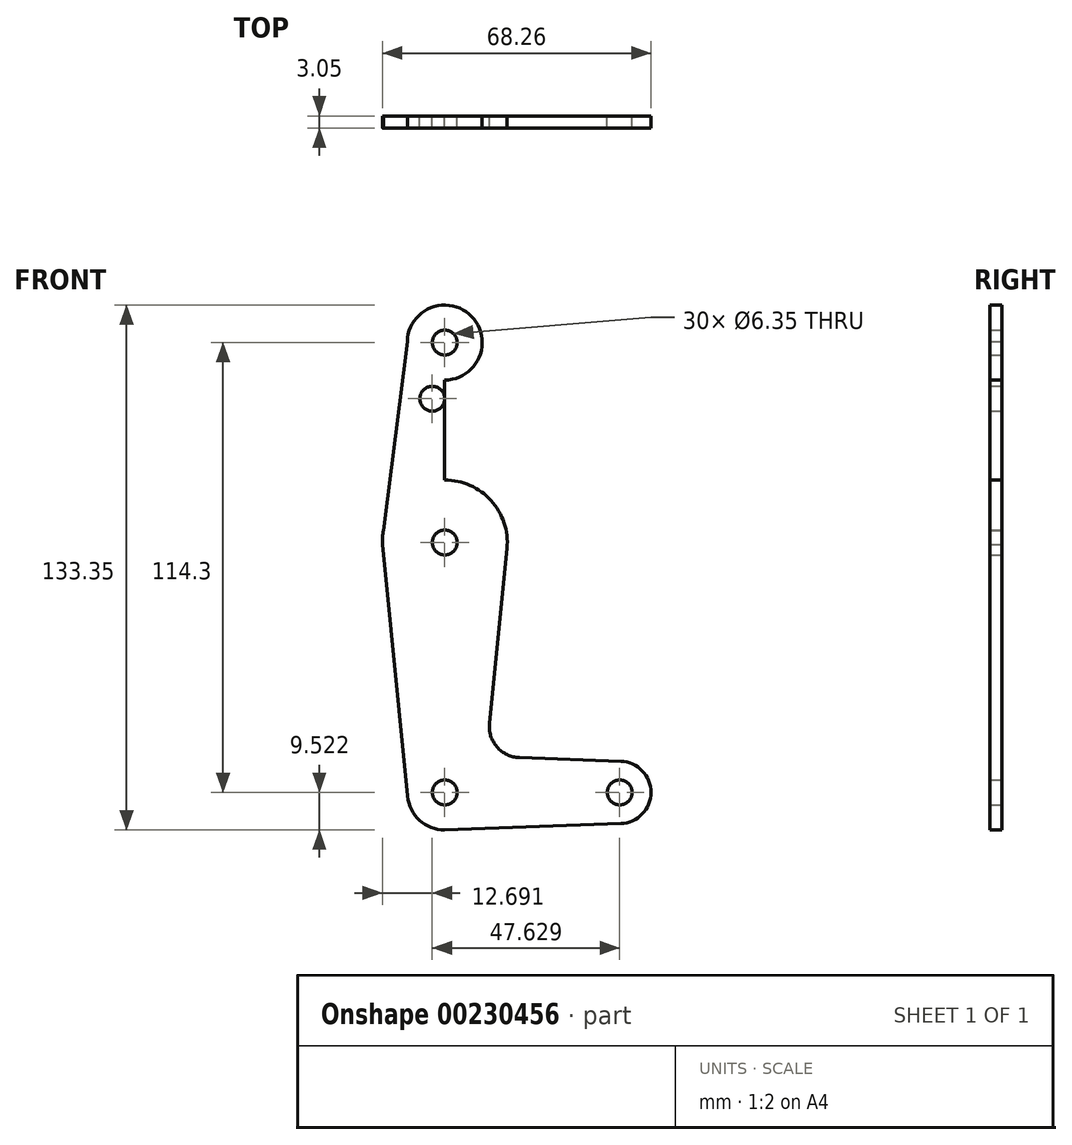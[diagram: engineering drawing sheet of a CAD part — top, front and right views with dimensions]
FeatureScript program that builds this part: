
annotation { "Feature Type Name" : "Feature", "Feature Type Description" : "" }
export const myFeature = defineFeature(function(context is Context, id is Id, definition is map)
    precondition{}
    {
        {
            var Q0;
            Q0=qCreatedBy(makeId("Front.planeOp"),FACE);
            var sketch = newSketch(context, id + "F0", { "sketchPlane" : qUnion([Q0])});
            skLineSegment(sketch, "E0", {"start": v(0, 73.32) * mm, "end": v(0, -40.98) * mm});
            skLineSegment(sketch, "E1", {"start": v(0, -40.98) * mm, "end": v(44.45, -40.98) * mm});
            skCircle(sketch, "E2", {"center": v(0, 73.32) * mm, "radius": 9.53 * mm});
            skCircle(sketch, "E3", {"center": v(0, -40.98) * mm, "radius": 9.53 * mm});
            skCircle(sketch, "E4", {"center": v(44.45, -40.98) * mm, "radius": 7.94 * mm});
            skLineSegment(sketch, "E5", {"start": v(0, -40.98) * mm, "end": v(0, 22.52) * mm});
            skCircle(sketch, "E6", {"center": v(0, 22.52) * mm, "radius": 15.88 * mm});
            skLineSegment(sketch, "E7", {"start": v(-9.52, 73.56) * mm, "end": v(-15.85, 23.48) * mm});
            skLineSegment(sketch, "E8", {"start": v(9.52, 73.56) * mm, "end": v(15.85, 23.48) * mm});
            skLineSegment(sketch, "E9", {"start": v(-15.87, 22.05) * mm, "end": v(-9.48, -41.92) * mm});
            skLineSegment(sketch, "E10", {"start": v(15.8, 21) * mm, "end": v(11.34, -23.39) * mm});
            skLineSegment(sketch, "E11", {"start": v(18.97, -32.13) * mm, "end": v(44.73, -33.05) * mm});
            skLineSegment(sketch, "E12", {"start": v(0, -50.5) * mm, "end": v(44.73, -48.91) * mm});
            skCircle(sketch, "E13", {"center": v(0, 73.32) * mm, "radius": 3.18 * mm});
            skCircle(sketch, "E14", {"center": v(0, 22.52) * mm, "radius": 3.18 * mm});
            skCircle(sketch, "E15", {"center": v(0, -40.98) * mm, "radius": 3.18 * mm});
            skCircle(sketch, "E16", {"center": v(44.45, -40.98) * mm, "radius": 3.18 * mm});
            skLineSegment(sketch, "E17", {"start": v(0, 22.52) * mm, "end": v(0, 59.05) * mm});
            skCircle(sketch, "E18", {"center": v(-3.18, 59.05) * mm, "radius": 3.18 * mm});
            skPoint(sketch, "E19.newPointB", {"position": v(0, -31.45) * mm});
            skArc(sketch, "E19.filletArc", {"start": v(11.34, -23.39) * mm, "mid": v(13.26, -29.41) * mm, "end": v(18.97, -32.13) * mm});
            skSolve(sketch);
        }
        {
            var Q0;
            {var subQ0=sQuery(id+"F0.wireOp",EDGE,"E12");var subQ1=sQuery(id+"F0.wireOp",EDGE,"E3");var subQ2=makeQuery(id+"F0.imprint","INTERSECT",VERTEX,{"disambiguationData":[OD(0.0)],"derivedFrom":[subQ1,subQ0]});Q0=makeQuery(id+"F0.imprint","IMPRINT",FACE,{"disambiguationData":[TD([[makeQuery(id+"F0.imprint","IMPRINT",EDGE,{"disambiguationData":[TD([[subQ2,-1.0]])],"derivedFrom":subQ1}),1.0]])]});}
            var Q1;
            {var subQ0=sQuery(id+"F0.wireOp",EDGE,"E8");var subQ1=sQuery(id+"F0.wireOp",EDGE,"E6");var subQ2=makeQuery(id+"F0.imprint","INTERSECT",VERTEX,{"disambiguationData":[OD(0.0)],"derivedFrom":[subQ1,subQ0]});Q1=makeQuery(id+"F0.imprint","IMPRINT",FACE,{"disambiguationData":[TD([[makeQuery(id+"F0.imprint","IMPRINT",EDGE,{"disambiguationData":[TD([[subQ2,-1.0]])],"derivedFrom":subQ1}),1.0]])]});}
            var Q2;
            {var subQ0=sQuery(id+"F0.wireOp",EDGE,"E7");var subQ1=sQuery(id+"F0.wireOp",EDGE,"E6");var subQ2=makeQuery(id+"F0.imprint","INTERSECT",VERTEX,{"disambiguationData":[OD(0.0)],"derivedFrom":[subQ1,subQ0]});Q2=makeQuery(id+"F0.imprint","IMPRINT",FACE,{"disambiguationData":[TD([[makeQuery(id+"F0.imprint","IMPRINT",EDGE,{"disambiguationData":[TD([[subQ2,1.0]])],"derivedFrom":subQ1}),1.0]])]});}
            var Q3;
            {var subQ0=sQuery(id+"F0.wireOp",EDGE,"E9");var subQ1=sQuery(id+"F0.wireOp",EDGE,"E6");var subQ2=makeQuery(id+"F0.imprint","INTERSECT",VERTEX,{"disambiguationData":[OD(0.0)],"derivedFrom":[subQ1,subQ0]});Q3=makeQuery(id+"F0.imprint","IMPRINT",FACE,{"disambiguationData":[TD([[makeQuery(id+"F0.imprint","IMPRINT",EDGE,{"disambiguationData":[TD([[subQ2,-1.0]])],"derivedFrom":subQ1}),1.0]])]});}
            var Q4;
            {var subQ0=sQuery(id+"F0.wireOp",EDGE,"E10");var subQ1=sQuery(id+"F0.wireOp",EDGE,"E6");var subQ2=makeQuery(id+"F0.imprint","INTERSECT",VERTEX,{"disambiguationData":[OD(0.0)],"derivedFrom":[subQ1,subQ0]});Q4=makeQuery(id+"F0.imprint","IMPRINT",FACE,{"disambiguationData":[TD([[makeQuery(id+"F0.imprint","IMPRINT",EDGE,{"disambiguationData":[TD([[subQ2,1.0]])],"derivedFrom":subQ1}),1.0]])]});}
            var Q5;
            {var subQ3=sQuery(id+"F0.wireOp",EDGE,"E17");var subQ7=sQuery(id+"F0.wireOp",EDGE,"E0");var subQ9=makeQuery(id+"F0.imprint","INTERSECT",VERTEX,{"derivedFrom":[subQ7,subQ3]});Q5=makeQuery(id+"F0.imprint","IMPRINT",FACE,{"disambiguationData":[TD([[makeQuery(id+"F0.imprint","IMPRINT",EDGE,{"disambiguationData":[TD([[subQ9,1.0]])],"derivedFrom":subQ7}),1.0]])]});}
            var Q6;
            {var subQ0=sQuery(id+"F0.wireOp",EDGE,"E4");var subQ1=sQuery(id+"F0.wireOp",EDGE,"E1");var subQ2=makeQuery(id+"F0.imprint","INTERSECT",VERTEX,{"derivedFrom":[subQ1,subQ0]});Q6=makeQuery(id+"F0.imprint","IMPRINT",FACE,{"disambiguationData":[TD([[makeQuery(id+"F0.imprint","IMPRINT",EDGE,{"disambiguationData":[TD([[subQ2,1.0]])],"derivedFrom":subQ1}),-1.0]])]});}
            var Q7;
            Q7=makeQuery(id+"F0.imprint","IMPRINT",FACE,{"disambiguationData":[TD([[makeQuery(id+"F0.imprint","IMPRINT",EDGE,{"derivedFrom":sQuery(id+"F0.wireOp",EDGE,"E13")}),-1.0]])]});
            var Q8;
            {var subQ0=sQuery(id+"F0.wireOp",EDGE,"E9");var subQ1=sQuery(id+"F0.wireOp",EDGE,"E3");var subQ2=makeQuery(id+"F0.imprint","INTERSECT",VERTEX,{"derivedFrom":[subQ1,subQ0]});Q8=makeQuery(id+"F0.imprint","IMPRINT",FACE,{"disambiguationData":[TD([[makeQuery(id+"F0.imprint","IMPRINT",EDGE,{"disambiguationData":[TD([[subQ2,1.0]])],"derivedFrom":subQ1}),-1.0]])]});}
            var Q9;
            Q9=makeQuery(id+"F0.imprint","IMPRINT",FACE,{"disambiguationData":[TD([[makeQuery(id+"F0.imprint","IMPRINT",EDGE,{"derivedFrom":sQuery(id+"F0.wireOp",EDGE,"E16")}),-1.0]])]});
            var Q10;
            Q10=makeQuery(id+"F0.imprint","IMPRINT",FACE,{"disambiguationData":[TD([[makeQuery(id+"F0.imprint","IMPRINT",EDGE,{"derivedFrom":sQuery(id+"F0.wireOp",EDGE,"E18")}),-1.0]])]});
            var Q11;
            {var subQ0=sQuery(id+"F0.wireOp",EDGE,"E11");Q11=makeQuery(id+"F0.imprint","IMPRINT",FACE,{"disambiguationData":[TD([[makeQuery(id+"F0.imprint","IMPRINT",EDGE,{"derivedFrom":subQ0}),-1.0]])]});}
            var Q12;
            {var subQ1=sQuery(id+"F0.wireOp",EDGE,"E6");var subQ7=sQuery(id+"F0.wireOp",EDGE,"E5");var subQ8=makeQuery(id+"F0.imprint","INTERSECT",VERTEX,{"derivedFrom":[subQ7,subQ1]});Q12=makeQuery(id+"F0.imprint","IMPRINT",FACE,{"disambiguationData":[TD([[makeQuery(id+"F0.imprint","IMPRINT",EDGE,{"disambiguationData":[TD([[subQ8,-1.0]])],"derivedFrom":subQ7}),-1.0]])]});}
            var Q13;
            {var subQ1=sQuery(id+"F0.wireOp",EDGE,"E6");var subQ3=sQuery(id+"F0.wireOp",EDGE,"E5");var subQ4=makeQuery(id+"F0.imprint","INTERSECT",VERTEX,{"derivedFrom":[subQ3,subQ1]});Q13=makeQuery(id+"F0.imprint","IMPRINT",FACE,{"disambiguationData":[TD([[makeQuery(id+"F0.imprint","IMPRINT",EDGE,{"disambiguationData":[TD([[subQ4,-1.0]])],"derivedFrom":subQ3}),1.0]])]});}
            var Q14;
            {var subQ3=sQuery(id+"F0.wireOp",EDGE,"E1");var subQ7=sQuery(id+"F0.wireOp",EDGE,"E15");var subQ8=makeQuery(id+"F0.imprint","INTERSECT",VERTEX,{"derivedFrom":[subQ3,subQ7]});Q14=makeQuery(id+"F0.imprint","IMPRINT",FACE,{"disambiguationData":[TD([[makeQuery(id+"F0.imprint","IMPRINT",EDGE,{"disambiguationData":[TD([[subQ8,-1.0]])],"derivedFrom":subQ3}),-1.0]])]});}
            var Q15;
            {var subQ0=sQuery(id+"F0.wireOp",EDGE,"E15");var subQ1=sQuery(id+"F0.wireOp",EDGE,"E1");var subQ2=makeQuery(id+"F0.imprint","INTERSECT",VERTEX,{"derivedFrom":[subQ1,subQ0]});Q15=makeQuery(id+"F0.imprint","IMPRINT",FACE,{"disambiguationData":[TD([[makeQuery(id+"F0.imprint","IMPRINT",EDGE,{"disambiguationData":[TD([[subQ2,-1.0]])],"derivedFrom":subQ1}),1.0]])]});}
            extrude(context, id + "F1", {"entities" : qUnion([Q0, Q1, Q2, Q3, Q4, Q5, Q6, Q7, Q8, Q9, Q10, Q11, Q12, Q13, Q14, Q15]), "depth" : 3.05 * mm});
        }
    });
